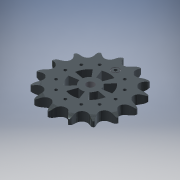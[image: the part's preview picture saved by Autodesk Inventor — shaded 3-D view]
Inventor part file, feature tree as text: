
AUTODESK INVENTOR PART (.ipt)
format: ipt  version: 2016 (Build 200138000, 138)  size: 633,856 bytes
history: native  units: mm
features: other x6, extrude x6, sketch x4, pattern_linear x1, pattern_circular x1
ambient origin geometry x8: Origin, YZ Plane, XZ Plane, XY Plane, X Axis, Y Axis, Z Axis, Center Point
bodies: Solid1 (feature_tree)
feature tree (18):
  other  "Theoretical Tooth Profile"
  other  "Tooth Profile"
  other  "Section Profile"
  other  "Shroud"
  other  "Strand"
  pattern_linear  "Strand Pattern"  Spacing1=2.490003mm  [1 undecoded]
  extrude  "Theoretical Tooth"  Depth=1.0mm
  extrude  "Tooth"  Depth=1.0mm
  pattern_circular  "Tooth Pattern"  [2 undecoded]
  other  "Timing Plane"
  extrude  "Extrusion4"  Depth=10.0mm TaperAngle=0.0deg
  extrude  "Extrusion5"  Depth=1.0mm
  extrude  "Extrusion6"  TaperAngle=360.0deg  [1 undecoded]
  extrude  "Extrusion7"  Depth=1.0mm
  sketch  "Sketch4"  dims[d0=61.083626mm]
  sketch  "Sketch5"  dims[d2=4.18879mm]
  sketch  "Sketch6"  dims[d3=4.29755mm]
  sketch  "Sketch7"  dims[d10=22.514747mm d11=2.490003mm d12=6.808mm d13=11.10555mm d14=11.914mm d18=10.0mm d19=0.0mm d20=150.0mm d21=360.0deg d23=3.81mm d28=0.0mm d29=0.0mm d30=7.2075mm d31=38.850402mm d32=7.2075mm d33=1.5875mm d34=12.7mm d36=90.0deg d37=90.0deg d38=10.0mm d40=13.92mm d42=0.0mm d43=3.60375mm d44=23.387412mm d45=17.3604mm d46=4.29755mm d47=10.0mm d48=0.0mm d49=0.0mm d50=10.0mm d51=10.0mm d53=30.0mm d87=40.0mm d88=15.0mm d89=30.0mm d92=6.981317mm d93=60.0mm d95=360.0deg d97=10.0mm d98=0.0mm d100=2.35mm d101=120.0mm d103=360.0deg d105=20.0mm d106=0.0mm d107=0.0mm d108=6.0mm d109=10.0mm d110=0.0mm d111=5.0mm d112=6.0mm d113=1.0mm d114=0.0mm]
note: 4 required parameter values undecoded (feature->parameter linkage not recoverable at this tier; creation-order binding heuristic only, values carry confidence <= 0.55)
